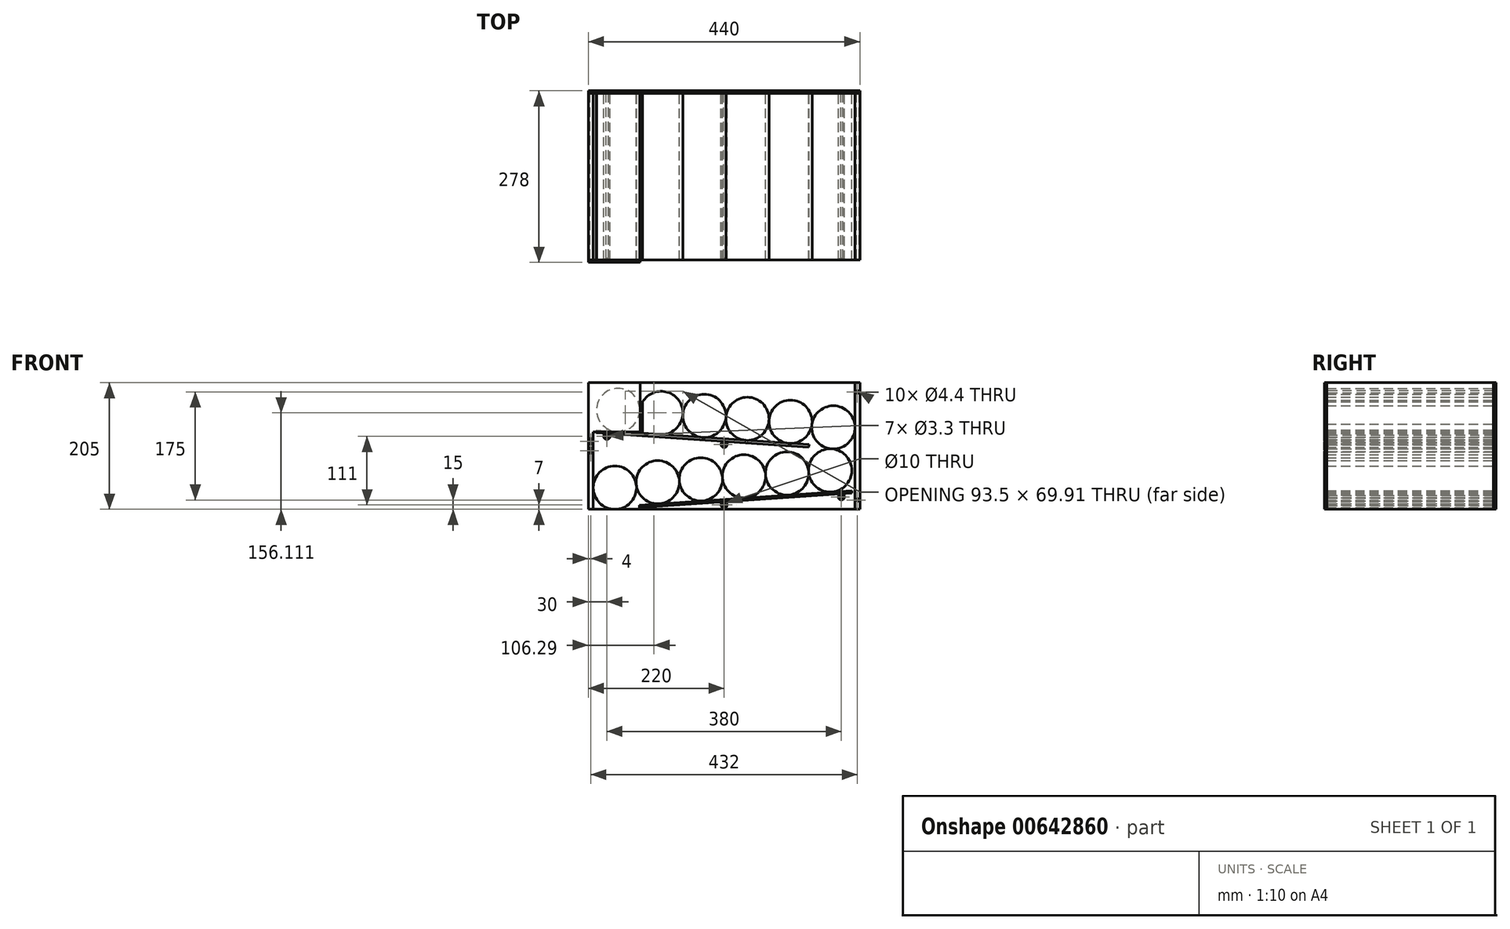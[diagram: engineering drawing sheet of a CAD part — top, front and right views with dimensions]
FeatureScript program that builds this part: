
annotation { "Feature Type Name" : "Feature", "Feature Type Description" : "" }
export const myFeature = defineFeature(function(context is Context, id is Id, definition is map)
    precondition{}
    {
        {
            var Q0;
            Q0=qCreatedBy(makeId("Front.planeOp"),FACE);
            var sketch = newSketch(context, id + "F0", { "sketchPlane" : qUnion([Q0])});
            skLineSegment(sketch, "E0.bottom", {"start": v(0, 0) * mm, "end": v(-440, 0) * mm});
            skLineSegment(sketch, "E0.top", {"start": v(0, 205) * mm, "end": v(-440, 205) * mm});
            skLineSegment(sketch, "E0.left", {"start": v(0, 0) * mm, "end": v(0, 205) * mm});
            skLineSegment(sketch, "E0.right", {"start": v(-440, 0) * mm, "end": v(-440, 205) * mm});
            skCircle(sketch, "E1", {"center": v(-397, 35) * mm, "radius": 35 * mm});
            skLineSegment(sketch, "E2", {"start": v(-357.47, 6.62) * mm, "end": v(-13.27, 30.17) * mm});
            skLineSegment(sketch, "E3", {"start": v(-440, 80) * mm, "end": v(-352, 80) * mm});
            skLineSegment(sketch, "E4", {"start": v(-352, 80) * mm, "end": v(-352, 0) * mm});
            skCircle(sketch, "E5", {"center": v(-327.55, 43.74) * mm, "radius": 35 * mm});
            skCircle(sketch, "E6", {"center": v(-257.71, 48.52) * mm, "radius": 35 * mm});
            skCircle(sketch, "E7", {"center": v(-187.87, 53.3) * mm, "radius": 35 * mm});
            skCircle(sketch, "E8", {"center": v(-118.04, 58.08) * mm, "radius": 35 * mm});
            skCircle(sketch, "E9", {"center": v(-48.2, 62.86) * mm, "radius": 35 * mm});
            skCircle(sketch, "E10", {"center": v(-43, 132.66) * mm, "radius": 35 * mm});
            skCircle(sketch, "E11", {"center": v(-112.4, 141.74) * mm, "radius": 35 * mm});
            skCircle(sketch, "E12", {"center": v(-182.25, 146.52) * mm, "radius": 35 * mm});
            skCircle(sketch, "E13", {"center": v(-252.08, 151.3) * mm, "radius": 35 * mm});
            skCircle(sketch, "E14", {"center": v(-321.92, 156.08) * mm, "radius": 35 * mm});
            skCircle(sketch, "E15", {"center": v(-391.76, 160.85) * mm, "radius": 35 * mm});
            skLineSegment(sketch, "E16", {"start": v(-426.73, 128.17) * mm, "end": v(-82.53, 104.62) * mm});
            skLineSegment(sketch, "E17", {"start": v(-440, 125) * mm, "end": v(-352, 125) * mm});
            skLineSegment(sketch, "E18", {"start": v(-352, 125) * mm, "end": v(-352, 205) * mm});
            skCircle(sketch, "E19", {"center": v(-220, 7) * mm, "radius": 5 * mm});
            skLineSegment(sketch, "E20", {"start": v(-8, 205) * mm, "end": v(-8, 0) * mm});
            skLineSegment(sketch, "E21", {"start": v(-432, 205) * mm, "end": v(-432, 0) * mm});
            skCircle(sketch, "E22", {"center": v(-30, 20) * mm, "radius": 5 * mm});
            skLineSegment(sketch, "E23", {"start": v(-427, 124.17) * mm, "end": v(-82.8, 100.62) * mm});
            skLineSegment(sketch, "E24", {"start": v(-427, 124.17) * mm, "end": v(-426.73, 128.17) * mm});
            skLineSegment(sketch, "E25", {"start": v(-357.2, 2.62) * mm, "end": v(-13, 26.17) * mm});
            skLineSegment(sketch, "E26", {"start": v(-13, 26.17) * mm, "end": v(-13.27, 30.17) * mm});
            skCircle(sketch, "E27", {"center": v(-220, 105) * mm, "radius": 5 * mm});
            skCircle(sketch, "E28", {"center": v(-410, 118) * mm, "radius": 5 * mm});
            skLineSegment(sketch, "E29", {"start": v(-82.53, 104.62) * mm, "end": v(-82.8, 100.62) * mm});
            skLineSegment(sketch, "E30", {"start": v(-357.47, 6.62) * mm, "end": v(-357.2, 2.62) * mm});
            skSolve(sketch);
        }
        {
            var Q0;
            {var subQ0=sQuery(id+"F0.wireOp",EDGE,"E0.right");var subQ1=sQuery(id+"F0.wireOp",EDGE,"E0.top");var subQ2=makeQuery(id+"F0.imprint","INTERSECT",VERTEX,{"derivedFrom":[subQ1,subQ0]});Q0=makeQuery(id+"F0.imprint","IMPRINT",FACE,{"disambiguationData":[TD([[makeQuery(id+"F0.imprint","IMPRINT",EDGE,{"disambiguationData":[TD([[subQ2,1.0]])],"derivedFrom":subQ1}),1.0]])]});}
            var Q1;
            {var subQ0=sQuery(id+"F0.wireOp",EDGE,"E3");var subQ1=sQuery(id+"F0.wireOp",EDGE,"E0.right");var subQ2=makeQuery(id+"F0.imprint","INTERSECT",VERTEX,{"derivedFrom":[subQ1,subQ0]});Q1=makeQuery(id+"F0.imprint","IMPRINT",FACE,{"disambiguationData":[TD([[makeQuery(id+"F0.imprint","IMPRINT",EDGE,{"disambiguationData":[TD([[subQ2,-1.0]])],"derivedFrom":subQ1}),-1.0]])]});}
            var Q2;
            {var subQ1=sQuery(id+"F0.wireOp",EDGE,"E0.right");var subQ6=sQuery(id+"F0.wireOp",EDGE,"E0.bottom");var subQ7=makeQuery(id+"F0.imprint","INTERSECT",VERTEX,{"derivedFrom":[subQ6,subQ1]});Q2=makeQuery(id+"F0.imprint","IMPRINT",FACE,{"disambiguationData":[TD([[makeQuery(id+"F0.imprint","IMPRINT",EDGE,{"disambiguationData":[TD([[subQ7,1.0]])],"derivedFrom":subQ6}),-1.0]])]});}
            var Q3;
            {var subQ4=sQuery(id+"F0.wireOp",EDGE,"E0.left");Q3=makeQuery(id+"F0.imprint","IMPRINT",FACE,{"disambiguationData":[TD([[makeQuery(id+"F0.imprint","IMPRINT",EDGE,{"derivedFrom":subQ4}),1.0]])]});}
            extrude(context, id + "F1", {"entities" : qUnion([Q0, Q1, Q2, Q3]), "depth" : 270 * mm, "offsetDistance" : 25 * mm});
        }
        {
            var Q0;
            {var subQ0=sQuery(id+"F0.wireOp",EDGE,"E15");var subQ1=makeQuery(id+"F0.imprint","INTERSECT",VERTEX,{"derivedFrom":[sQuery(id+"F0.wireOp",EDGE,"E14"),subQ0]});Q0=makeQuery(id+"F0.imprint","IMPRINT",FACE,{"disambiguationData":[TD([[makeQuery(id+"F0.imprint","IMPRINT",EDGE,{"disambiguationData":[TD([[subQ1,1.0]])],"derivedFrom":subQ0}),1.0]])]});}
            var Q1;
            {var subQ0=sQuery(id+"F0.wireOp",EDGE,"E18");var subQ1=sQuery(id+"F0.wireOp",EDGE,"E14");var subQ2=makeQuery(id+"F0.imprint","INTERSECT",VERTEX,{"disambiguationData":[OD(1.0)],"derivedFrom":[subQ1,subQ0]});Q1=makeQuery(id+"F0.imprint","IMPRINT",FACE,{"disambiguationData":[TD([[makeQuery(id+"F0.imprint","IMPRINT",EDGE,{"disambiguationData":[TD([[subQ2,-1.0]])],"derivedFrom":subQ1}),1.0]])]});}
            var Q2;
            {var subQ0=sQuery(id+"F0.wireOp",EDGE,"E14");var subQ1=makeQuery(id+"F0.imprint","INTERSECT",VERTEX,{"derivedFrom":[subQ0,sQuery(id+"F0.wireOp",EDGE,"E15")]});Q2=makeQuery(id+"F0.imprint","IMPRINT",FACE,{"disambiguationData":[TD([[makeQuery(id+"F0.imprint","IMPRINT",EDGE,{"disambiguationData":[TD([[subQ1,1.0]])],"derivedFrom":subQ0}),1.0]])]});}
            var Q3;
            {var subQ0=sQuery(id+"F0.wireOp",EDGE,"E13");var subQ1=makeQuery(id+"F0.imprint","INTERSECT",VERTEX,{"derivedFrom":[subQ0,sQuery(id+"F0.wireOp",EDGE,"E16")]});Q3=makeQuery(id+"F0.imprint","IMPRINT",FACE,{"disambiguationData":[TD([[makeQuery(id+"F0.imprint","IMPRINT",EDGE,{"disambiguationData":[TD([[subQ1,1.0]])],"derivedFrom":subQ0}),1.0]])]});}
            var Q4;
            {var subQ0=sQuery(id+"F0.wireOp",EDGE,"E12");var subQ1=makeQuery(id+"F0.imprint","INTERSECT",VERTEX,{"derivedFrom":[subQ0,sQuery(id+"F0.wireOp",EDGE,"E16")]});Q4=makeQuery(id+"F0.imprint","IMPRINT",FACE,{"disambiguationData":[TD([[makeQuery(id+"F0.imprint","IMPRINT",EDGE,{"disambiguationData":[TD([[subQ1,1.0]])],"derivedFrom":subQ0}),1.0]])]});}
            var Q5;
            {var subQ0=sQuery(id+"F0.wireOp",EDGE,"E11");var subQ1=makeQuery(id+"F0.imprint","INTERSECT",VERTEX,{"derivedFrom":[subQ0,sQuery(id+"F0.wireOp",EDGE,"E16")]});Q5=makeQuery(id+"F0.imprint","IMPRINT",FACE,{"disambiguationData":[TD([[makeQuery(id+"F0.imprint","IMPRINT",EDGE,{"disambiguationData":[TD([[subQ1,1.0]])],"derivedFrom":subQ0}),1.0]])]});}
            var Q6;
            {var subQ0=sQuery(id+"F0.wireOp",EDGE,"E20");var subQ1=sQuery(id+"F0.wireOp",EDGE,"E10");var subQ2=makeQuery(id+"F0.imprint","INTERSECT",VERTEX,{"disambiguationData":[OD(0.0)],"derivedFrom":[subQ1,subQ0]});Q6=makeQuery(id+"F0.imprint","IMPRINT",FACE,{"disambiguationData":[TD([[makeQuery(id+"F0.imprint","IMPRINT",EDGE,{"disambiguationData":[TD([[subQ2,1.0]])],"derivedFrom":subQ1}),1.0]])]});}
            var Q7;
            {var subQ0=sQuery(id+"F0.wireOp",EDGE,"E9");var subQ1=makeQuery(id+"F0.imprint","INTERSECT",VERTEX,{"derivedFrom":[sQuery(id+"F0.wireOp",EDGE,"E8"),subQ0]});Q7=makeQuery(id+"F0.imprint","IMPRINT",FACE,{"disambiguationData":[TD([[makeQuery(id+"F0.imprint","IMPRINT",EDGE,{"disambiguationData":[TD([[subQ1,1.0]])],"derivedFrom":subQ0}),1.0]])]});}
            var Q8;
            {var subQ0=sQuery(id+"F0.wireOp",EDGE,"E8");var subQ1=makeQuery(id+"F0.imprint","INTERSECT",VERTEX,{"derivedFrom":[sQuery(id+"F0.wireOp",EDGE,"E7"),subQ0]});Q8=makeQuery(id+"F0.imprint","IMPRINT",FACE,{"disambiguationData":[TD([[makeQuery(id+"F0.imprint","IMPRINT",EDGE,{"disambiguationData":[TD([[subQ1,1.0]])],"derivedFrom":subQ0}),1.0]])]});}
            var Q9;
            {var subQ0=sQuery(id+"F0.wireOp",EDGE,"E7");var subQ1=makeQuery(id+"F0.imprint","INTERSECT",VERTEX,{"derivedFrom":[sQuery(id+"F0.wireOp",EDGE,"E6"),subQ0]});Q9=makeQuery(id+"F0.imprint","IMPRINT",FACE,{"disambiguationData":[TD([[makeQuery(id+"F0.imprint","IMPRINT",EDGE,{"disambiguationData":[TD([[subQ1,1.0]])],"derivedFrom":subQ0}),1.0]])]});}
            var Q10;
            {var subQ0=sQuery(id+"F0.wireOp",EDGE,"E6");var subQ1=makeQuery(id+"F0.imprint","INTERSECT",VERTEX,{"derivedFrom":[sQuery(id+"F0.wireOp",EDGE,"E5"),subQ0]});Q10=makeQuery(id+"F0.imprint","IMPRINT",FACE,{"disambiguationData":[TD([[makeQuery(id+"F0.imprint","IMPRINT",EDGE,{"disambiguationData":[TD([[subQ1,1.0]])],"derivedFrom":subQ0}),1.0]])]});}
            var Q11;
            {var subQ0=sQuery(id+"F0.wireOp",EDGE,"E5");var subQ1=sQuery(id+"F0.wireOp",EDGE,"E4");var subQ2=makeQuery(id+"F0.imprint","INTERSECT",VERTEX,{"disambiguationData":[OD(0.0)],"derivedFrom":[subQ1,subQ0]});Q11=makeQuery(id+"F0.imprint","IMPRINT",FACE,{"disambiguationData":[TD([[makeQuery(id+"F0.imprint","IMPRINT",EDGE,{"disambiguationData":[TD([[subQ2,-1.0]])],"derivedFrom":subQ1}),1.0]])]});}
            var Q12;
            {var subQ0=sQuery(id+"F0.wireOp",EDGE,"E1");var subQ1=makeQuery(id+"F0.imprint","INTERSECT",VERTEX,{"derivedFrom":[subQ0,sQuery(id+"F0.wireOp",EDGE,"E21")]});Q12=makeQuery(id+"F0.imprint","IMPRINT",FACE,{"disambiguationData":[TD([[makeQuery(id+"F0.imprint","IMPRINT",EDGE,{"disambiguationData":[TD([[subQ1,1.0]])],"derivedFrom":subQ0}),1.0]])]});}
            var Q13;
            {var subQ0=sQuery(id+"F0.wireOp",EDGE,"E5");var subQ1=sQuery(id+"F0.wireOp",EDGE,"E4");var subQ2=makeQuery(id+"F0.imprint","INTERSECT",VERTEX,{"disambiguationData":[OD(0.0)],"derivedFrom":[subQ1,subQ0]});Q13=makeQuery(id+"F0.imprint","IMPRINT",FACE,{"disambiguationData":[TD([[makeQuery(id+"F0.imprint","IMPRINT",EDGE,{"disambiguationData":[TD([[subQ2,-1.0]])],"derivedFrom":subQ1}),-1.0]])]});}
            extrude(context, id + "F2", {"entities" : qUnion([Q0, Q1, Q2, Q3, Q4, Q5, Q6, Q7, Q8, Q9, Q10, Q11, Q12, Q13]), "depth" : 270 * mm, "offsetDistance" : 25 * mm});
        }
        {
            var Q0;
            {var subQ5=sQuery(id+"F0.wireOp",EDGE,"E29");Q0=makeQuery(id+"F0.imprint","IMPRINT",FACE,{"disambiguationData":[TD([[makeQuery(id+"F0.imprint","IMPRINT",EDGE,{"derivedFrom":subQ5}),-1.0]])]});}
            var Q1;
            {var subQ0=sQuery(id+"F0.wireOp",EDGE,"E24");var subQ1=sQuery(id+"F0.wireOp",EDGE,"E16");var subQ2=makeQuery(id+"F0.imprint","INTERSECT",VERTEX,{"derivedFrom":[subQ1,subQ0]});Q1=makeQuery(id+"F0.imprint","IMPRINT",FACE,{"disambiguationData":[TD([[makeQuery(id+"F0.imprint","IMPRINT",EDGE,{"disambiguationData":[TD([[subQ2,-1.0]])],"derivedFrom":subQ1}),-1.0]])]});}
            var Q2;
            {var subQ0=sQuery(id+"F0.wireOp",EDGE,"E30");Q2=makeQuery(id+"F0.imprint","IMPRINT",FACE,{"disambiguationData":[TD([[makeQuery(id+"F0.imprint","IMPRINT",EDGE,{"derivedFrom":subQ0}),1.0]])]});}
            var Q3;
            {var subQ0=sQuery(id+"F0.wireOp",EDGE,"E26");Q3=makeQuery(id+"F0.imprint","IMPRINT",FACE,{"disambiguationData":[TD([[makeQuery(id+"F0.imprint","IMPRINT",EDGE,{"derivedFrom":subQ0}),1.0]])]});}
            extrude(context, id + "F3", {"entities" : qUnion([Q0, Q1, Q2, Q3]), "depth" : 270 * mm, "offsetDistance" : 25 * mm});
        }
        {
            var Q0;
            Q0=makeQuery(id+"F0.imprint","IMPRINT",FACE,{"disambiguationData":[TD([[makeQuery(id+"F0.imprint","IMPRINT",EDGE,{"derivedFrom":sQuery(id+"F0.wireOp",EDGE,"E28")}),1.0]])]});
            var Q1;
            Q1=makeQuery(id+"F0.imprint","IMPRINT",FACE,{"disambiguationData":[TD([[makeQuery(id+"F0.imprint","IMPRINT",EDGE,{"derivedFrom":sQuery(id+"F0.wireOp",EDGE,"E27")}),1.0]])]});
            var Q2;
            Q2=makeQuery(id+"F0.imprint","IMPRINT",FACE,{"disambiguationData":[TD([[makeQuery(id+"F0.imprint","IMPRINT",EDGE,{"derivedFrom":sQuery(id+"F0.wireOp",EDGE,"E19")}),1.0]])]});
            var Q3;
            Q3=makeQuery(id+"F0.imprint","IMPRINT",FACE,{"disambiguationData":[TD([[makeQuery(id+"F0.imprint","IMPRINT",EDGE,{"derivedFrom":sQuery(id+"F0.wireOp",EDGE,"E22")}),1.0]])]});
            extrude(context, id + "F4", {"entities" : qUnion([Q0, Q1, Q2, Q3]), "depth" : 270 * mm, "offsetDistance" : 25 * mm});
        }
        {
            var Q0;
            {var subQ4=sQuery(id+"F0.wireOp",EDGE,"E0.left");Q0=makeQuery(id+"F0.imprint","IMPRINT",FACE,{"disambiguationData":[TD([[makeQuery(id+"F0.imprint","IMPRINT",EDGE,{"derivedFrom":subQ4}),1.0]])]});}
            var Q1;
            {var subQ8=sQuery(id+"F0.wireOp",EDGE,"E18");var subQ11=sQuery(id+"F0.wireOp",EDGE,"E0.top");var subQ15=makeQuery(id+"F0.imprint","INTERSECT",VERTEX,{"derivedFrom":[subQ11,subQ8]});Q1=makeQuery(id+"F0.imprint","IMPRINT",FACE,{"disambiguationData":[TD([[makeQuery(id+"F0.imprint","IMPRINT",EDGE,{"disambiguationData":[TD([[subQ15,1.0]])],"derivedFrom":subQ11}),1.0]])]});}
            var Q2;
            {var subQ0=sQuery(id+"F0.wireOp",EDGE,"E20");var subQ1=sQuery(id+"F0.wireOp",EDGE,"E10");var subQ2=makeQuery(id+"F0.imprint","INTERSECT",VERTEX,{"disambiguationData":[OD(0.0)],"derivedFrom":[subQ1,subQ0]});Q2=makeQuery(id+"F0.imprint","IMPRINT",FACE,{"disambiguationData":[TD([[makeQuery(id+"F0.imprint","IMPRINT",EDGE,{"disambiguationData":[TD([[subQ2,1.0]])],"derivedFrom":subQ1}),1.0]])]});}
            var Q3;
            {var subQ0=sQuery(id+"F0.wireOp",EDGE,"E11");var subQ1=makeQuery(id+"F0.imprint","INTERSECT",VERTEX,{"derivedFrom":[subQ0,sQuery(id+"F0.wireOp",EDGE,"E16")]});Q3=makeQuery(id+"F0.imprint","IMPRINT",FACE,{"disambiguationData":[TD([[makeQuery(id+"F0.imprint","IMPRINT",EDGE,{"disambiguationData":[TD([[subQ1,1.0]])],"derivedFrom":subQ0}),1.0]])]});}
            var Q4;
            {var subQ0=sQuery(id+"F0.wireOp",EDGE,"E12");var subQ1=makeQuery(id+"F0.imprint","INTERSECT",VERTEX,{"derivedFrom":[subQ0,sQuery(id+"F0.wireOp",EDGE,"E16")]});Q4=makeQuery(id+"F0.imprint","IMPRINT",FACE,{"disambiguationData":[TD([[makeQuery(id+"F0.imprint","IMPRINT",EDGE,{"disambiguationData":[TD([[subQ1,1.0]])],"derivedFrom":subQ0}),1.0]])]});}
            var Q5;
            {var subQ0=sQuery(id+"F0.wireOp",EDGE,"E13");var subQ1=makeQuery(id+"F0.imprint","INTERSECT",VERTEX,{"derivedFrom":[subQ0,sQuery(id+"F0.wireOp",EDGE,"E16")]});Q5=makeQuery(id+"F0.imprint","IMPRINT",FACE,{"disambiguationData":[TD([[makeQuery(id+"F0.imprint","IMPRINT",EDGE,{"disambiguationData":[TD([[subQ1,1.0]])],"derivedFrom":subQ0}),1.0]])]});}
            var Q6;
            {var subQ0=sQuery(id+"F0.wireOp",EDGE,"E18");var subQ1=sQuery(id+"F0.wireOp",EDGE,"E14");var subQ2=makeQuery(id+"F0.imprint","INTERSECT",VERTEX,{"disambiguationData":[OD(1.0)],"derivedFrom":[subQ1,subQ0]});Q6=makeQuery(id+"F0.imprint","IMPRINT",FACE,{"disambiguationData":[TD([[makeQuery(id+"F0.imprint","IMPRINT",EDGE,{"disambiguationData":[TD([[subQ2,-1.0]])],"derivedFrom":subQ1}),1.0]])]});}
            var Q7;
            {var subQ0=sQuery(id+"F0.wireOp",EDGE,"E14");var subQ1=makeQuery(id+"F0.imprint","INTERSECT",VERTEX,{"derivedFrom":[subQ0,sQuery(id+"F0.wireOp",EDGE,"E15")]});Q7=makeQuery(id+"F0.imprint","IMPRINT",FACE,{"disambiguationData":[TD([[makeQuery(id+"F0.imprint","IMPRINT",EDGE,{"disambiguationData":[TD([[subQ1,1.0]])],"derivedFrom":subQ0}),1.0]])]});}
            var Q8;
            {var subQ9=sQuery(id+"F0.wireOp",EDGE,"E18");var subQ11=sQuery(id+"F0.wireOp",EDGE,"E0.top");var subQ12=makeQuery(id+"F0.imprint","INTERSECT",VERTEX,{"derivedFrom":[subQ11,subQ9]});Q8=makeQuery(id+"F0.imprint","IMPRINT",FACE,{"disambiguationData":[TD([[makeQuery(id+"F0.imprint","IMPRINT",EDGE,{"disambiguationData":[TD([[subQ12,-1.0]])],"derivedFrom":subQ11}),1.0]])]});}
            var Q9;
            {var subQ0=sQuery(id+"F0.wireOp",EDGE,"E0.right");var subQ1=sQuery(id+"F0.wireOp",EDGE,"E0.top");var subQ2=makeQuery(id+"F0.imprint","INTERSECT",VERTEX,{"derivedFrom":[subQ1,subQ0]});Q9=makeQuery(id+"F0.imprint","IMPRINT",FACE,{"disambiguationData":[TD([[makeQuery(id+"F0.imprint","IMPRINT",EDGE,{"disambiguationData":[TD([[subQ2,1.0]])],"derivedFrom":subQ1}),1.0]])]});}
            var Q10;
            {var subQ0=sQuery(id+"F0.wireOp",EDGE,"E3");var subQ1=sQuery(id+"F0.wireOp",EDGE,"E0.right");var subQ2=makeQuery(id+"F0.imprint","INTERSECT",VERTEX,{"derivedFrom":[subQ1,subQ0]});Q10=makeQuery(id+"F0.imprint","IMPRINT",FACE,{"disambiguationData":[TD([[makeQuery(id+"F0.imprint","IMPRINT",EDGE,{"disambiguationData":[TD([[subQ2,-1.0]])],"derivedFrom":subQ1}),-1.0]])]});}
            var Q11;
            {var subQ1=sQuery(id+"F0.wireOp",EDGE,"E0.right");var subQ6=sQuery(id+"F0.wireOp",EDGE,"E0.bottom");var subQ7=makeQuery(id+"F0.imprint","INTERSECT",VERTEX,{"derivedFrom":[subQ6,subQ1]});Q11=makeQuery(id+"F0.imprint","IMPRINT",FACE,{"disambiguationData":[TD([[makeQuery(id+"F0.imprint","IMPRINT",EDGE,{"disambiguationData":[TD([[subQ7,1.0]])],"derivedFrom":subQ6}),-1.0]])]});}
            var Q12;
            {var subQ0=sQuery(id+"F0.wireOp",EDGE,"E24");var subQ1=sQuery(id+"F0.wireOp",EDGE,"E16");var subQ2=makeQuery(id+"F0.imprint","INTERSECT",VERTEX,{"derivedFrom":[subQ1,subQ0]});Q12=makeQuery(id+"F0.imprint","IMPRINT",FACE,{"disambiguationData":[TD([[makeQuery(id+"F0.imprint","IMPRINT",EDGE,{"disambiguationData":[TD([[subQ2,-1.0]])],"derivedFrom":subQ1}),-1.0]])]});}
            var Q13;
            {var subQ0=sQuery(id+"F0.wireOp",EDGE,"E15");var subQ1=makeQuery(id+"F0.imprint","INTERSECT",VERTEX,{"derivedFrom":[sQuery(id+"F0.wireOp",EDGE,"E14"),subQ0]});Q13=makeQuery(id+"F0.imprint","IMPRINT",FACE,{"disambiguationData":[TD([[makeQuery(id+"F0.imprint","IMPRINT",EDGE,{"disambiguationData":[TD([[subQ1,1.0]])],"derivedFrom":subQ0}),1.0]])]});}
            var Q14;
            {var subQ0=sQuery(id+"F0.wireOp",EDGE,"E15");var subQ1=sQuery(id+"F0.wireOp",EDGE,"E14");var subQ2=makeQuery(id+"F0.imprint","INTERSECT",VERTEX,{"derivedFrom":[subQ1,subQ0]});Q14=makeQuery(id+"F0.imprint","IMPRINT",FACE,{"disambiguationData":[TD([[makeQuery(id+"F0.imprint","IMPRINT",EDGE,{"disambiguationData":[TD([[subQ2,-1.0]])],"derivedFrom":subQ1}),-1.0]])]});}
            var Q15;
            {var subQ0=sQuery(id+"F0.wireOp",EDGE,"E18");var subQ6=sQuery(id+"F0.wireOp",EDGE,"E14");var subQ9=makeQuery(id+"F0.imprint","INTERSECT",VERTEX,{"disambiguationData":[OD(1.0)],"derivedFrom":[subQ6,subQ0]});Q15=makeQuery(id+"F0.imprint","IMPRINT",FACE,{"disambiguationData":[TD([[makeQuery(id+"F0.imprint","IMPRINT",EDGE,{"disambiguationData":[TD([[subQ9,-1.0]])],"derivedFrom":subQ6}),-1.0]])]});}
            var Q16;
            {var subQ0=sQuery(id+"F0.wireOp",EDGE,"E16");var subQ1=sQuery(id+"F0.wireOp",EDGE,"E13");var subQ2=makeQuery(id+"F0.imprint","INTERSECT",VERTEX,{"derivedFrom":[subQ1,subQ0]});Q16=makeQuery(id+"F0.imprint","IMPRINT",FACE,{"disambiguationData":[TD([[makeQuery(id+"F0.imprint","IMPRINT",EDGE,{"disambiguationData":[TD([[subQ2,1.0]])],"derivedFrom":subQ1}),-1.0]])]});}
            var Q17;
            {var subQ0=sQuery(id+"F0.wireOp",EDGE,"E16");var subQ1=sQuery(id+"F0.wireOp",EDGE,"E12");var subQ2=makeQuery(id+"F0.imprint","INTERSECT",VERTEX,{"derivedFrom":[subQ1,subQ0]});Q17=makeQuery(id+"F0.imprint","IMPRINT",FACE,{"disambiguationData":[TD([[makeQuery(id+"F0.imprint","IMPRINT",EDGE,{"disambiguationData":[TD([[subQ2,1.0]])],"derivedFrom":subQ1}),-1.0]])]});}
            var Q18;
            {var subQ0=sQuery(id+"F0.wireOp",EDGE,"E16");var subQ1=sQuery(id+"F0.wireOp",EDGE,"E11");var subQ2=makeQuery(id+"F0.imprint","INTERSECT",VERTEX,{"derivedFrom":[subQ1,subQ0]});Q18=makeQuery(id+"F0.imprint","IMPRINT",FACE,{"disambiguationData":[TD([[makeQuery(id+"F0.imprint","IMPRINT",EDGE,{"disambiguationData":[TD([[subQ2,1.0]])],"derivedFrom":subQ1}),-1.0]])]});}
            var Q19;
            Q19=makeQuery(id+"F0.imprint","IMPRINT",FACE,{"disambiguationData":[TD([[makeQuery(id+"F0.imprint","IMPRINT",EDGE,{"derivedFrom":sQuery(id+"F0.wireOp",EDGE,"E27")}),1.0]])]});
            var Q20;
            Q20=makeQuery(id+"F0.imprint","IMPRINT",FACE,{"disambiguationData":[TD([[makeQuery(id+"F0.imprint","IMPRINT",EDGE,{"derivedFrom":sQuery(id+"F0.wireOp",EDGE,"E28")}),1.0]])]});
            var Q21;
            {var subQ5=sQuery(id+"F0.wireOp",EDGE,"E29");Q21=makeQuery(id+"F0.imprint","IMPRINT",FACE,{"disambiguationData":[TD([[makeQuery(id+"F0.imprint","IMPRINT",EDGE,{"derivedFrom":subQ5}),-1.0]])]});}
            var Q22;
            {var subQ10=sQuery(id+"F0.wireOp",EDGE,"E19");Q22=makeQuery(id+"F0.imprint","IMPRINT",FACE,{"disambiguationData":[TD([[makeQuery(id+"F0.imprint","IMPRINT",EDGE,{"derivedFrom":subQ10}),-1.0]])]});}
            var Q23;
            Q23=makeQuery(id+"F0.imprint","IMPRINT",FACE,{"disambiguationData":[TD([[makeQuery(id+"F0.imprint","IMPRINT",EDGE,{"derivedFrom":sQuery(id+"F0.wireOp",EDGE,"E22")}),1.0]])]});
            var Q24;
            {var subQ0=sQuery(id+"F0.wireOp",EDGE,"E26");Q24=makeQuery(id+"F0.imprint","IMPRINT",FACE,{"disambiguationData":[TD([[makeQuery(id+"F0.imprint","IMPRINT",EDGE,{"derivedFrom":subQ0}),1.0]])]});}
            var Q25;
            {var subQ0=sQuery(id+"F0.wireOp",EDGE,"E30");Q25=makeQuery(id+"F0.imprint","IMPRINT",FACE,{"disambiguationData":[TD([[makeQuery(id+"F0.imprint","IMPRINT",EDGE,{"derivedFrom":subQ0}),1.0]])]});}
            var Q26;
            {var subQ0=sQuery(id+"F0.wireOp",EDGE,"E30");Q26=makeQuery(id+"F0.imprint","IMPRINT",FACE,{"disambiguationData":[TD([[makeQuery(id+"F0.imprint","IMPRINT",EDGE,{"derivedFrom":subQ0}),-1.0]])]});}
            var Q27;
            {var subQ0=sQuery(id+"F0.wireOp",EDGE,"E21");var subQ1=sQuery(id+"F0.wireOp",EDGE,"E0.bottom");var subQ2=makeQuery(id+"F0.imprint","INTERSECT",VERTEX,{"derivedFrom":[subQ1,subQ0]});Q27=makeQuery(id+"F0.imprint","IMPRINT",FACE,{"disambiguationData":[TD([[makeQuery(id+"F0.imprint","IMPRINT",EDGE,{"disambiguationData":[TD([[subQ2,1.0]])],"derivedFrom":subQ1}),-1.0]])]});}
            var Q28;
            {var subQ1=sQuery(id+"F0.wireOp",EDGE,"E1");var subQ7=sQuery(id+"F0.wireOp",EDGE,"E21");var subQ9=makeQuery(id+"F0.imprint","INTERSECT",VERTEX,{"derivedFrom":[subQ1,subQ7]});Q28=makeQuery(id+"F0.imprint","IMPRINT",FACE,{"disambiguationData":[TD([[makeQuery(id+"F0.imprint","IMPRINT",EDGE,{"disambiguationData":[TD([[subQ9,1.0]])],"derivedFrom":subQ1}),-1.0]])]});}
            var Q29;
            {var subQ0=sQuery(id+"F0.wireOp",EDGE,"E1");var subQ1=makeQuery(id+"F0.imprint","INTERSECT",VERTEX,{"derivedFrom":[subQ0,sQuery(id+"F0.wireOp",EDGE,"E21")]});Q29=makeQuery(id+"F0.imprint","IMPRINT",FACE,{"disambiguationData":[TD([[makeQuery(id+"F0.imprint","IMPRINT",EDGE,{"disambiguationData":[TD([[subQ1,1.0]])],"derivedFrom":subQ0}),1.0]])]});}
            var Q30;
            {var subQ0=sQuery(id+"F0.wireOp",EDGE,"E5");var subQ1=sQuery(id+"F0.wireOp",EDGE,"E4");var subQ2=makeQuery(id+"F0.imprint","INTERSECT",VERTEX,{"disambiguationData":[OD(0.0)],"derivedFrom":[subQ1,subQ0]});Q30=makeQuery(id+"F0.imprint","IMPRINT",FACE,{"disambiguationData":[TD([[makeQuery(id+"F0.imprint","IMPRINT",EDGE,{"disambiguationData":[TD([[subQ2,-1.0]])],"derivedFrom":subQ1}),-1.0]])]});}
            var Q31;
            {var subQ0=sQuery(id+"F0.wireOp",EDGE,"E5");var subQ1=sQuery(id+"F0.wireOp",EDGE,"E4");var subQ2=makeQuery(id+"F0.imprint","INTERSECT",VERTEX,{"disambiguationData":[OD(0.0)],"derivedFrom":[subQ1,subQ0]});Q31=makeQuery(id+"F0.imprint","IMPRINT",FACE,{"disambiguationData":[TD([[makeQuery(id+"F0.imprint","IMPRINT",EDGE,{"disambiguationData":[TD([[subQ2,-1.0]])],"derivedFrom":subQ1}),1.0]])]});}
            var Q32;
            {var subQ0=sQuery(id+"F0.wireOp",EDGE,"E6");var subQ1=makeQuery(id+"F0.imprint","INTERSECT",VERTEX,{"derivedFrom":[sQuery(id+"F0.wireOp",EDGE,"E5"),subQ0]});Q32=makeQuery(id+"F0.imprint","IMPRINT",FACE,{"disambiguationData":[TD([[makeQuery(id+"F0.imprint","IMPRINT",EDGE,{"disambiguationData":[TD([[subQ1,1.0]])],"derivedFrom":subQ0}),1.0]])]});}
            var Q33;
            {var subQ0=sQuery(id+"F0.wireOp",EDGE,"E7");var subQ1=makeQuery(id+"F0.imprint","INTERSECT",VERTEX,{"derivedFrom":[sQuery(id+"F0.wireOp",EDGE,"E6"),subQ0]});Q33=makeQuery(id+"F0.imprint","IMPRINT",FACE,{"disambiguationData":[TD([[makeQuery(id+"F0.imprint","IMPRINT",EDGE,{"disambiguationData":[TD([[subQ1,1.0]])],"derivedFrom":subQ0}),1.0]])]});}
            var Q34;
            {var subQ0=sQuery(id+"F0.wireOp",EDGE,"E8");var subQ1=makeQuery(id+"F0.imprint","INTERSECT",VERTEX,{"derivedFrom":[sQuery(id+"F0.wireOp",EDGE,"E7"),subQ0]});Q34=makeQuery(id+"F0.imprint","IMPRINT",FACE,{"disambiguationData":[TD([[makeQuery(id+"F0.imprint","IMPRINT",EDGE,{"disambiguationData":[TD([[subQ1,1.0]])],"derivedFrom":subQ0}),1.0]])]});}
            var Q35;
            {var subQ0=sQuery(id+"F0.wireOp",EDGE,"E9");var subQ1=makeQuery(id+"F0.imprint","INTERSECT",VERTEX,{"derivedFrom":[sQuery(id+"F0.wireOp",EDGE,"E8"),subQ0]});Q35=makeQuery(id+"F0.imprint","IMPRINT",FACE,{"disambiguationData":[TD([[makeQuery(id+"F0.imprint","IMPRINT",EDGE,{"disambiguationData":[TD([[subQ1,1.0]])],"derivedFrom":subQ0}),1.0]])]});}
            var Q36;
            {var subQ0=sQuery(id+"F0.wireOp",EDGE,"E8");var subQ1=sQuery(id+"F0.wireOp",EDGE,"E2");var subQ2=makeQuery(id+"F0.imprint","INTERSECT",VERTEX,{"derivedFrom":[subQ1,subQ0]});Q36=makeQuery(id+"F0.imprint","IMPRINT",FACE,{"disambiguationData":[TD([[makeQuery(id+"F0.imprint","IMPRINT",EDGE,{"disambiguationData":[TD([[subQ2,-1.0]])],"derivedFrom":subQ1}),1.0]])]});}
            var Q37;
            {var subQ0=sQuery(id+"F0.wireOp",EDGE,"E7");var subQ1=sQuery(id+"F0.wireOp",EDGE,"E2");var subQ2=makeQuery(id+"F0.imprint","INTERSECT",VERTEX,{"derivedFrom":[subQ1,subQ0]});Q37=makeQuery(id+"F0.imprint","IMPRINT",FACE,{"disambiguationData":[TD([[makeQuery(id+"F0.imprint","IMPRINT",EDGE,{"disambiguationData":[TD([[subQ2,-1.0]])],"derivedFrom":subQ1}),1.0]])]});}
            var Q38;
            {var subQ0=sQuery(id+"F0.wireOp",EDGE,"E6");var subQ1=sQuery(id+"F0.wireOp",EDGE,"E2");var subQ2=makeQuery(id+"F0.imprint","INTERSECT",VERTEX,{"derivedFrom":[subQ1,subQ0]});Q38=makeQuery(id+"F0.imprint","IMPRINT",FACE,{"disambiguationData":[TD([[makeQuery(id+"F0.imprint","IMPRINT",EDGE,{"disambiguationData":[TD([[subQ2,-1.0]])],"derivedFrom":subQ1}),1.0]])]});}
            var Q39;
            {var subQ0=sQuery(id+"F0.wireOp",EDGE,"E5");var subQ1=sQuery(id+"F0.wireOp",EDGE,"E2");var subQ2=makeQuery(id+"F0.imprint","INTERSECT",VERTEX,{"derivedFrom":[subQ1,subQ0]});Q39=makeQuery(id+"F0.imprint","IMPRINT",FACE,{"disambiguationData":[TD([[makeQuery(id+"F0.imprint","IMPRINT",EDGE,{"disambiguationData":[TD([[subQ2,-1.0]])],"derivedFrom":subQ1}),1.0]])]});}
            var Q40;
            {var subQ0=sQuery(id+"F0.wireOp",EDGE,"E4");var subQ1=sQuery(id+"F0.wireOp",EDGE,"E2");var subQ2=makeQuery(id+"F0.imprint","INTERSECT",VERTEX,{"derivedFrom":[subQ1,subQ0]});Q40=makeQuery(id+"F0.imprint","IMPRINT",FACE,{"disambiguationData":[TD([[makeQuery(id+"F0.imprint","IMPRINT",EDGE,{"disambiguationData":[TD([[subQ2,-1.0]])],"derivedFrom":subQ1}),1.0]])]});}
            var Q41;
            {var subQ11=sQuery(id+"F0.wireOp",EDGE,"E27");Q41=makeQuery(id+"F0.imprint","IMPRINT",FACE,{"disambiguationData":[TD([[makeQuery(id+"F0.imprint","IMPRINT",EDGE,{"derivedFrom":subQ11}),-1.0]])]});}
            extrude(context, id + "F5", {"entities" : qUnion([Q0, Q1, Q2, Q3, Q4, Q5, Q6, Q7, Q8, Q9, Q10, Q11, Q12, Q13, Q14, Q15, Q16, Q17, Q18, Q19, Q20, Q21, Q22, Q23, Q24, Q25, Q26, Q27, Q28, Q29, Q30, Q31, Q32, Q33, Q34, Q35, Q36, Q37, Q38, Q39, Q40, Q41]), "oppositeDirection" : true, "depth" : 4 * mm, "offsetDistance" : 25 * mm});
        }
        {
            var Q0;
            Q0=makeQuery(id+"F1.opExtrude","CAP_FACE",FACE,{"disambiguationData":[OSD([sQuery(id+"F0.wireOp",EDGE,"E0.bottom"),sQuery(id+"F0.wireOp",EDGE,"E0.top"),sQuery(id+"F0.wireOp",EDGE,"E0.right"),sQuery(id+"F0.wireOp",EDGE,"E21")])],"isStart":false});
            var sketch = newSketch(context, id + "F6", { "sketchPlane" : qUnion([Q0])});
            skLineSegment(sketch, "E31.bottom", {"start": v(-440, 205) * mm, "end": v(0, 205) * mm});
            skLineSegment(sketch, "E31.top", {"start": v(-440, 0) * mm, "end": v(0, 0) * mm});
            skLineSegment(sketch, "E31.left", {"start": v(-440, 205) * mm, "end": v(-440, 0) * mm});
            skLineSegment(sketch, "E31.right", {"start": v(0, 205) * mm, "end": v(0, 0) * mm});
            skLineSegment(sketch, "E32.bottom", {"start": v(-440, 205) * mm, "end": v(-356, 205) * mm});
            skLineSegment(sketch, "E32.top", {"start": v(-440, 125) * mm, "end": v(-356, 125) * mm});
            skLineSegment(sketch, "E32.left", {"start": v(-440, 205) * mm, "end": v(-440, 125) * mm});
            skLineSegment(sketch, "E32.right", {"start": v(-356, 205) * mm, "end": v(-356, 125) * mm});
            skLineSegment(sketch, "E33.bottom", {"start": v(-440, 0) * mm, "end": v(-356, 0) * mm});
            skLineSegment(sketch, "E33.top", {"start": v(-440, 80) * mm, "end": v(-356, 80) * mm});
            skLineSegment(sketch, "E33.left", {"start": v(-440, 0) * mm, "end": v(-440, 80) * mm});
            skLineSegment(sketch, "E33.right", {"start": v(-356, 0) * mm, "end": v(-356, 80) * mm});
            skSolve(sketch);
        }
        {
            var Q0;
            Q0=makeQuery(id+"F6.imprint","IMPRINT",FACE,{"disambiguationData":[TD([[makeQuery(id+"F6.imprint","IMPRINT",EDGE,{"derivedFrom":sQuery(id+"F6.wireOp",EDGE,"E31.bottom")}),-1.0]])]});
            var Q1;
            {var subQ0=sQuery(id+"F6.wireOp",EDGE,"E31.left");Q1=makeQuery(id+"F6.imprint","IMPRINT",FACE,{"disambiguationData":[TD([[makeQuery(id+"F6.imprint","IMPRINT",EDGE,{"derivedFrom":subQ0}),-1.0]])]});}
            extrude(context, id + "F7", {"entities" : qUnion([Q0, Q1]), "depth" : 4 * mm, "offsetDistance" : 25 * mm});
        }
        {
            var Q0;
            Q0=makeQuery(id+"F7.opExtrude","CAP_FACE",FACE,{"disambiguationData":[OSD([sQuery(id+"F6.wireOp",EDGE,"E31.bottom"),sQuery(id+"F6.wireOp",EDGE,"E31.top"),sQuery(id+"F6.wireOp",EDGE,"E31.left"),sQuery(id+"F6.wireOp",EDGE,"E31.right"),sQuery(id+"F6.wireOp",EDGE,"E32.top"),sQuery(id+"F6.wireOp",EDGE,"E32.right"),sQuery(id+"F6.wireOp",EDGE,"E33.top"),sQuery(id+"F6.wireOp",EDGE,"E33.right")])],"isStart":false});
            var sketch = newSketch(context, id + "F8", { "sketchPlane" : qUnion([Q0])});
            skPoint(sketch, "E34", {"position": v(-436, 110) * mm});
            skPoint(sketch, "E35", {"position": v(-436, 95) * mm});
            skPoint(sketch, "E36", {"position": v(-4, 190) * mm});
            skPoint(sketch, "E37", {"position": v(-4, 15) * mm});
            skSolve(sketch);
        }
        {
            var Q0;
            Q0=sQuery(id+"F8.wireOp",VERTEX,"E34");
            var Q1;
            Q1=sQuery(id+"F8.wireOp",VERTEX,"E35");
            var Q2;
            Q2=sQuery(id+"F8.wireOp",VERTEX,"E37");
            var Q3;
            Q3=sQuery(id+"F8.wireOp",VERTEX,"E36");
            var Q4;
            Q4=makeQuery(id+"F1.opExtrude","SWEPT_BODY",BODY,{"disambiguationData":[OSD([sQuery(id+"F0.wireOp",EDGE,"E0.bottom"),sQuery(id+"F0.wireOp",EDGE,"E0.top"),sQuery(id+"F0.wireOp",EDGE,"E0.right"),sQuery(id+"F0.wireOp",EDGE,"E21")])]});
            var Q5;
            Q5=makeQuery(id+"F5.opExtrude","SWEPT_BODY",BODY,{"disambiguationData":[OSD([sQuery(id+"F0.wireOp",EDGE,"E0.bottom"),sQuery(id+"F0.wireOp",EDGE,"E0.top"),sQuery(id+"F0.wireOp",EDGE,"E0.left"),sQuery(id+"F0.wireOp",EDGE,"E0.right"),sQuery(id+"F0.wireOp",EDGE,"E15"),sQuery(id+"F0.wireOp",EDGE,"E16"),sQuery(id+"F0.wireOp",EDGE,"E17"),sQuery(id+"F0.wireOp",EDGE,"E19")])]});
            var Q6;
            Q6=makeQuery(id+"F7.opExtrude","SWEPT_BODY",BODY,{"disambiguationData":[OSD([sQuery(id+"F6.wireOp",EDGE,"E31.bottom"),sQuery(id+"F6.wireOp",EDGE,"E31.top"),sQuery(id+"F6.wireOp",EDGE,"E31.left"),sQuery(id+"F6.wireOp",EDGE,"E31.right"),sQuery(id+"F6.wireOp",EDGE,"E32.top"),sQuery(id+"F6.wireOp",EDGE,"E32.right"),sQuery(id+"F6.wireOp",EDGE,"E33.top"),sQuery(id+"F6.wireOp",EDGE,"E33.right")])]});
            var Q7;
            Q7=makeQuery(id+"F1.opExtrude","SWEPT_BODY",BODY,{"disambiguationData":[OSD([sQuery(id+"F0.wireOp",EDGE,"E0.bottom"),sQuery(id+"F0.wireOp",EDGE,"E0.top"),sQuery(id+"F0.wireOp",EDGE,"E0.left"),sQuery(id+"F0.wireOp",EDGE,"E10"),sQuery(id+"F0.wireOp",EDGE,"E20")])]});
            hole(context, id + "F9", {"style" : HoleStyle.SIMPLE, "endStyle" : HoleEndStyle.THROUGH, "standardTappedOrClearance" : lookupTablePath({ "standard" : "ISO", "engagement" : "75%", "pitch" : "0.7 mm", "size" : "M4", "type" : "Tapped" }), "standardBlindInLast" : lookupTablePath({ "standard" : "ISO", "engagement" : "75%", "pitch" : "0.7 mm", "size" : "M4", "type" : "Tapped" }), "holeDiameter" : 3.3 * mm, "majorDiameter" : 4 * mm, "showTappedDepth" : true, "tappedDepth" : 25 * mm, "tapClearance" : 3, "locations" : qUnion([Q0, Q1, Q2, Q3]), "scope" : qUnion([Q4, Q5, Q6, Q7])});
        }
        {
            var Q0;
            Q0=sQuery(id+"F8.wireOp",VERTEX,"E34");
            var Q1;
            Q1=sQuery(id+"F8.wireOp",VERTEX,"E35");
            var Q2;
            Q2=sQuery(id+"F8.wireOp",VERTEX,"E37");
            var Q3;
            Q3=sQuery(id+"F8.wireOp",VERTEX,"E36");
            var Q4;
            Q4=makeQuery(id+"F1.opExtrude","SWEPT_BODY",BODY,{"disambiguationData":[OSD([sQuery(id+"F0.wireOp",EDGE,"E0.bottom"),sQuery(id+"F0.wireOp",EDGE,"E0.top"),sQuery(id+"F0.wireOp",EDGE,"E0.left"),sQuery(id+"F0.wireOp",EDGE,"E10"),sQuery(id+"F0.wireOp",EDGE,"E20")])]});
            var Q5;
            Q5=makeQuery(id+"F1.opExtrude","SWEPT_BODY",BODY,{"disambiguationData":[OSD([sQuery(id+"F0.wireOp",EDGE,"E0.bottom"),sQuery(id+"F0.wireOp",EDGE,"E0.top"),sQuery(id+"F0.wireOp",EDGE,"E0.right"),sQuery(id+"F0.wireOp",EDGE,"E21")])]});
            var Q6;
            Q6=makeQuery(id+"F5.opExtrude","SWEPT_BODY",BODY,{"disambiguationData":[OSD([sQuery(id+"F0.wireOp",EDGE,"E0.bottom"),sQuery(id+"F0.wireOp",EDGE,"E0.top"),sQuery(id+"F0.wireOp",EDGE,"E0.left"),sQuery(id+"F0.wireOp",EDGE,"E0.right"),sQuery(id+"F0.wireOp",EDGE,"E15"),sQuery(id+"F0.wireOp",EDGE,"E16"),sQuery(id+"F0.wireOp",EDGE,"E17"),sQuery(id+"F0.wireOp",EDGE,"E19")])]});
            var Q7;
            Q7=makeQuery(id+"F7.opExtrude","SWEPT_BODY",BODY,{"disambiguationData":[OSD([sQuery(id+"F6.wireOp",EDGE,"E31.bottom"),sQuery(id+"F6.wireOp",EDGE,"E31.top"),sQuery(id+"F6.wireOp",EDGE,"E31.left"),sQuery(id+"F6.wireOp",EDGE,"E31.right"),sQuery(id+"F6.wireOp",EDGE,"E32.top"),sQuery(id+"F6.wireOp",EDGE,"E32.right"),sQuery(id+"F6.wireOp",EDGE,"E33.top"),sQuery(id+"F6.wireOp",EDGE,"E33.right")])]});
            hole(context, id + "F10", {"style" : HoleStyle.C_SINK, "endStyle" : HoleEndStyle.THROUGH, "standardTappedOrClearance" : lookupTablePath({ "standard" : "ISO", "fit" : "Normal", "size" : "M4", "type" : "Clearance" }), "standardBlindInLast" : lookupTablePath({ "fit" : "Standard", "standard" : "ISO", "size" : "M4", "type" : "Clearance" }), "holeDiameter" : 4.4 * mm, "cSinkDiameter" : 8.96 * mm, "cSinkAngle" : 90 * degree, "majorDiameter" : 4 * mm, "isTappedThrough" : true, "tappedDepth" : 25 * mm, "tapClearance" : 3, "locations" : qUnion([Q0, Q1, Q2, Q3]), "scope" : qUnion([Q4, Q5, Q6, Q7])});
        }
        {
            var Q0;
            Q0=makeQuery(id+"F8.imprint","IMPRINT",FACE,{"disambiguationData":[TD([[makeQuery(id+"F8.imprint","IMPRINT",EDGE,{"derivedFrom":makeQuery(id+"F7.opExtrude","CAP_EDGE",EDGE,{"disambiguationData":[OSD([sQuery(id+"F6.wireOp",EDGE,"E31.bottom")])],"isStart":false})}),-1.0]])]});
            var sketch = newSketch(context, id + "F11", { "sketchPlane" : qUnion([Q0])});
            skPoint(sketch, "E38", {"position": v(-220, 105) * mm});
            skPoint(sketch, "E39", {"position": v(-410, 118) * mm});
            skPoint(sketch, "E40", {"position": v(-220, 7) * mm});
            skPoint(sketch, "E41", {"position": v(-30, 20) * mm});
            skSolve(sketch);
        }
        {
            var Q0;
            Q0=sQuery(id+"F11.wireOp",VERTEX,"E39");
            var Q1;
            Q1=sQuery(id+"F11.wireOp",VERTEX,"E38");
            var Q2;
            Q2=sQuery(id+"F11.wireOp",VERTEX,"E40");
            var Q3;
            Q3=sQuery(id+"F11.wireOp",VERTEX,"E41");
            var Q4;
            Q4=makeQuery(id+"F5.opExtrude","SWEPT_BODY",BODY,{"disambiguationData":[OSD([sQuery(id+"F0.wireOp",EDGE,"E0.bottom"),sQuery(id+"F0.wireOp",EDGE,"E0.top"),sQuery(id+"F0.wireOp",EDGE,"E0.left"),sQuery(id+"F0.wireOp",EDGE,"E0.right"),sQuery(id+"F0.wireOp",EDGE,"E15"),sQuery(id+"F0.wireOp",EDGE,"E16"),sQuery(id+"F0.wireOp",EDGE,"E17"),sQuery(id+"F0.wireOp",EDGE,"E19")])]});
            var Q5;
            Q5=makeQuery(id+"F7.opExtrude","SWEPT_BODY",BODY,{"disambiguationData":[OSD([sQuery(id+"F6.wireOp",EDGE,"E31.bottom"),sQuery(id+"F6.wireOp",EDGE,"E31.top"),sQuery(id+"F6.wireOp",EDGE,"E31.left"),sQuery(id+"F6.wireOp",EDGE,"E31.right"),sQuery(id+"F6.wireOp",EDGE,"E32.top"),sQuery(id+"F6.wireOp",EDGE,"E32.right"),sQuery(id+"F6.wireOp",EDGE,"E33.top"),sQuery(id+"F6.wireOp",EDGE,"E33.right")])]});
            var Q6;
            Q6=makeQuery(id+"F4.opExtrude","SWEPT_BODY",BODY,{"disambiguationData":[OSD([sQuery(id+"F0.wireOp",EDGE,"E19")])]});
            var Q7;
            Q7=makeQuery(id+"F4.opExtrude","SWEPT_BODY",BODY,{"disambiguationData":[OSD([sQuery(id+"F0.wireOp",EDGE,"E22")])]});
            var Q8;
            Q8=makeQuery(id+"F4.opExtrude","SWEPT_BODY",BODY,{"disambiguationData":[OSD([sQuery(id+"F0.wireOp",EDGE,"E27")])]});
            var Q9;
            Q9=makeQuery(id+"F4.opExtrude","SWEPT_BODY",BODY,{"disambiguationData":[OSD([sQuery(id+"F0.wireOp",EDGE,"E28")])]});
            hole(context, id + "F12", {"style" : HoleStyle.C_SINK, "endStyle" : HoleEndStyle.THROUGH, "standardTappedOrClearance" : lookupTablePath({ "standard" : "ISO", "engagement" : "75%", "pitch" : "0.7 mm", "size" : "M4", "type" : "Tapped" }), "standardBlindInLast" : lookupTablePath({ "standard" : "ISO", "engagement" : "75%", "pitch" : "0.7 mm", "size" : "M4", "type" : "Tapped" }), "holeDiameter" : 3.3 * mm, "cSinkDiameter" : 8.96 * mm, "cSinkAngle" : 90 * degree, "majorDiameter" : 4 * mm, "showTappedDepth" : true, "tappedDepth" : 25 * mm, "tapClearance" : 3, "locations" : qUnion([Q0, Q1, Q2, Q3]), "scope" : qUnion([Q4, Q5, Q6, Q7, Q8, Q9])});
        }
    });
